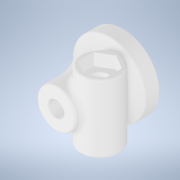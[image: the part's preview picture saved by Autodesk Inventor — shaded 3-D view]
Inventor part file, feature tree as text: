
AUTODESK INVENTOR PART (.ipt)
format: ipt  version: 2020 (Build 240168000, 168)  size: 481,792 bytes
history: native  units: mm
features: sketch x6, fillet x5, extrude x4, hole x2, projected_geometry x2
ambient origin geometry x8: Origin, YZ Plane, XZ Plane, XY Plane, X Axis, Y Axis, Z Axis, Center Point
bodies: Solid1 (feature_tree)
feature tree (19):
  extrude  "Extrusion1"  Depth=3.0mm TaperAngle=0.0deg
  extrude  "Extrusion2"  Depth=10.0mm TaperAngle=0.0deg
  fillet  "Fillet1"  Radius=10.0mm
  extrude  "Extrusion3"  Depth=8.0mm
  fillet  "Fillet3"  Radius=3.2mm
  fillet  "Fillet4"  Radius=4.0mm
  fillet  "Fillet5"  Radius=5.5mm
  hole  "Hole1"  [1 undecoded]
  hole  "Hole2"  [1 undecoded]
  extrude  "Extrusion4"  Depth=0.25mm
  fillet  "Fillet7"  Radius=2.5mm
  sketch  "Sketch1"  dims[d0=15.0mm d1=3.0mm d2=0.0mm]
  sketch  "Sketch2"  dims[d3=8.0mm d4=11.0mm d5=0.0mm d6=10.0mm]
  sketch  "Sketch3"  dims[d7=3.2mm d8=6.0mm d9=4.0mm d10=2.0mm d11=90.0deg d12=8.0mm d13=20.594885mm d14=8.0mm d15=3.2mm d16=4.0mm d17=5.5mm]
  sketch  "Sketch4"  dims[d18=14.0mm d19=0.0mm d21=1.0mm]
  sketch  "Sketch5"  dims[d22=0.5mm d23=0.5mm]
  sketch  "Sketch6"  dims[d24=3.2mm d25=6.0mm d26=4.0mm d27=2.0mm d28=90.0deg d29=8.0mm d30=20.594885mm d31=5.75mm d32=2.5mm d33=0.0mm d35=0.25mm d36=0.5mm d37=0.872665mm d38=0.5mm d39=0.872665mm]
  projected_geometry  "Project Cut Edges1"
  projected_geometry  "Project Cut Edges2"
note: 2 required parameter values undecoded (feature->parameter linkage not recoverable at this tier; creation-order binding heuristic only, values carry confidence <= 0.55)
